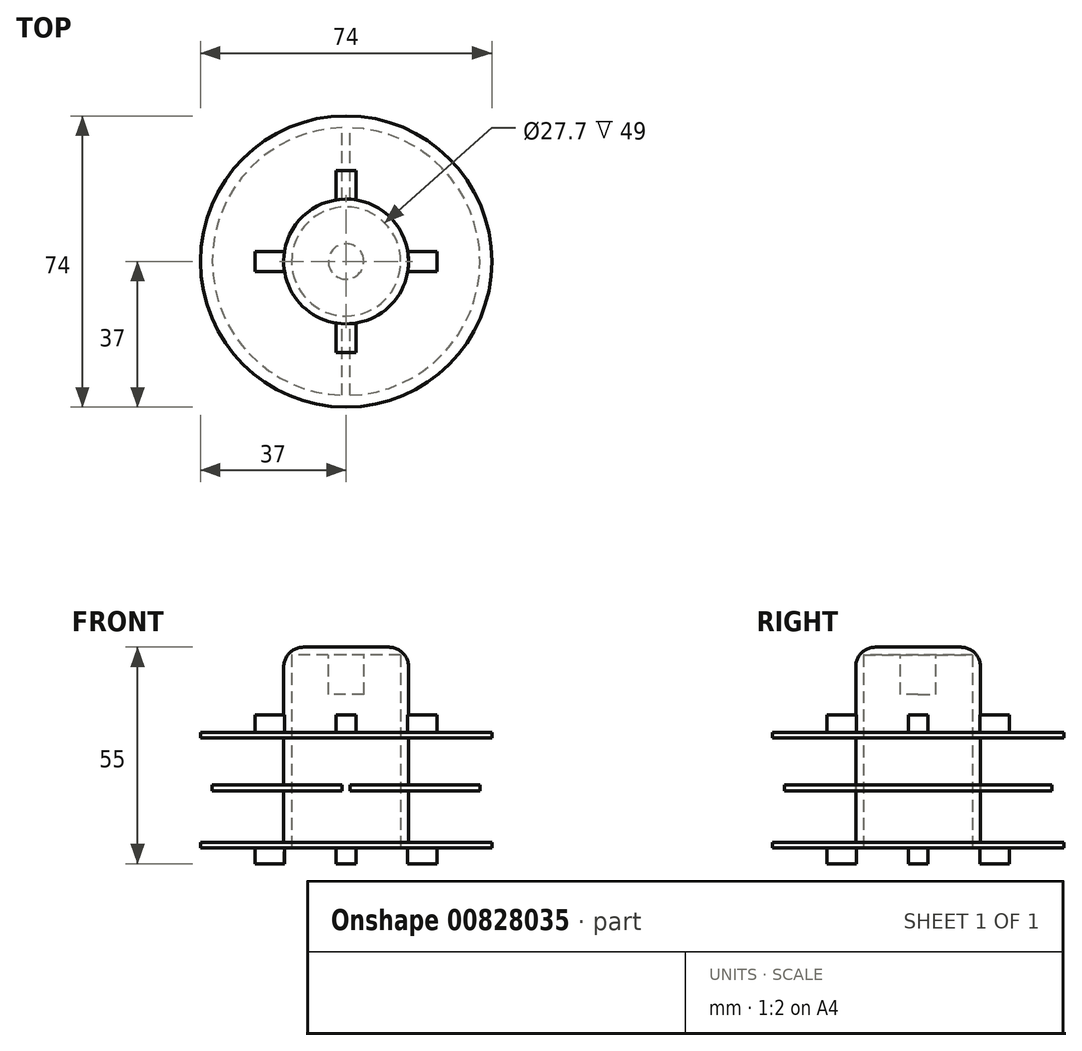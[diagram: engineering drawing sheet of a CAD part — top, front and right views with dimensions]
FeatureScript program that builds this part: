
annotation { "Feature Type Name" : "Feature", "Feature Type Description" : "" }
export const myFeature = defineFeature(function(context is Context, id is Id, definition is map)
    precondition{}
    {
        {
            var Q0;
            Q0=qCreatedBy(makeId("Top.planeOp"),FACE);
            var sketch = newSketch(context, id + "F0", { "sketchPlane" : qUnion([Q0])});
            skCircle(sketch, "E0", {"center": v(0, 0) * mm, "radius": 37 * mm});
            skCircle(sketch, "E1.0", {"center": v(0, 0) * mm, "radius": 34 * mm});
            skCircle(sketch, "E2", {"center": v(0, 0) * mm, "radius": 15.85 * mm});
            skLineSegment(sketch, "E3.top", {"start": v(0, 23.13) * mm, "end": v(-2.5, 23.13) * mm});
            skLineSegment(sketch, "E3.right", {"start": v(-2.5, 15.65) * mm, "end": v(-2.5, 23.13) * mm});
            skLineSegment(sketch, "E4.MirrorCS", {"start": v(0, 23.13) * mm, "end": v(2.5, 23.13) * mm});
            skLineSegment(sketch, "E5.MirrorCS", {"start": v(2.5, 15.65) * mm, "end": v(2.5, 23.13) * mm});
            skLineSegment(sketch, "E6.1.0", {"start": v(-15.65, -2.5) * mm, "end": v(-23.13, -2.5) * mm});
            skLineSegment(sketch, "E6.1.1", {"start": v(-23.13, 0) * mm, "end": v(-23.13, -2.5) * mm});
            skLineSegment(sketch, "E6.1.2", {"start": v(-23.13, 0) * mm, "end": v(-23.13, 2.5) * mm});
            skLineSegment(sketch, "E6.1.3", {"start": v(-15.65, 2.5) * mm, "end": v(-23.13, 2.5) * mm});
            skLineSegment(sketch, "E6.2.0", {"start": v(2.5, -15.65) * mm, "end": v(2.5, -23.13) * mm});
            skLineSegment(sketch, "E6.2.1", {"start": v(0, -23.13) * mm, "end": v(2.5, -23.13) * mm});
            skLineSegment(sketch, "E6.2.2", {"start": v(0, -23.13) * mm, "end": v(-2.5, -23.13) * mm});
            skLineSegment(sketch, "E6.2.3", {"start": v(-2.5, -15.65) * mm, "end": v(-2.5, -23.13) * mm});
            skLineSegment(sketch, "E6.3.0", {"start": v(15.65, 2.5) * mm, "end": v(23.13, 2.5) * mm});
            skLineSegment(sketch, "E6.3.1", {"start": v(23.13, 0) * mm, "end": v(23.13, 2.5) * mm});
            skLineSegment(sketch, "E6.3.2", {"start": v(23.13, 0) * mm, "end": v(23.13, -2.5) * mm});
            skLineSegment(sketch, "E6.3.3", {"start": v(15.65, -2.5) * mm, "end": v(23.13, -2.5) * mm});
            skPoint(sketch, "E7.orphan", {"position": v(-2.5, 15.85) * mm});
            skPoint(sketch, "E8.orphan", {"position": v(2.5, 15.85) * mm});
            skPoint(sketch, "E9.orphan", {"position": v(15.85, 2.5) * mm});
            skPoint(sketch, "E10.orphan", {"position": v(-15.85, 2.5) * mm});
            skPoint(sketch, "E11.orphan", {"position": v(-15.85, -2.5) * mm});
            skPoint(sketch, "E12.orphan", {"position": v(-2.5, -15.85) * mm});
            skPoint(sketch, "E13.orphan", {"position": v(2.5, -15.85) * mm});
            skPoint(sketch, "E14.orphan", {"position": v(15.85, -2.5) * mm});
            skSolve(sketch);
        }
        {
            var Q0;
            {var subQ0=sQuery(id+"F0.wireOp",EDGE,"E2");var subQ4=makeQuery(id+"F0.imprint","INTERSECT",VERTEX,{"derivedFrom":[subQ0,sQuery(id+"F0.wireOp",EDGE,"E5.MirrorCS")]});Q0=makeQuery(id+"F0.imprint","IMPRINT",FACE,{"disambiguationData":[TD([[makeQuery(id+"F0.imprint","IMPRINT",EDGE,{"disambiguationData":[TD([[subQ4,1.0]])],"derivedFrom":subQ0}),1.0]])]});}
            extrude(context, id + "F1", {"entities" : qUnion([Q0]), "depth" : 51 * mm, "offsetDistance" : 25 * mm});
        }
        {
            var Q0;
            Q0=makeQuery(id+"F0.imprint","IMPRINT",FACE,{"disambiguationData":[TD([[makeQuery(id+"F0.imprint","IMPRINT",EDGE,{"derivedFrom":sQuery(id+"F0.wireOp",EDGE,"E0")}),1.0]])]});
            var Q1;
            Q1=makeQuery(id+"F0.imprint","IMPRINT",FACE,{"disambiguationData":[TD([[makeQuery(id+"F0.imprint","IMPRINT",EDGE,{"derivedFrom":sQuery(id+"F0.wireOp",EDGE,"E1.0")}),1.0]])]});
            var Q2;
            {var subQ0=sQuery(id+"F0.wireOp",EDGE,"E6.1.0");Q2=makeQuery(id+"F0.imprint","IMPRINT",FACE,{"disambiguationData":[TD([[makeQuery(id+"F0.imprint","IMPRINT",EDGE,{"derivedFrom":subQ0}),-1.0]])]});}
            var Q3;
            Q3=makeQuery(id+"F0.imprint","IMPRINT",FACE,{"disambiguationData":[TD([[makeQuery(id+"F0.imprint","IMPRINT",EDGE,{"derivedFrom":sQuery(id+"F0.wireOp",EDGE,"E3.top")}),1.0]])]});
            var Q4;
            {var subQ0=sQuery(id+"F0.wireOp",EDGE,"E3.left");Q4=makeQuery(id+"F0.imprint","IMPRINT",FACE,{"disambiguationData":[TD([[makeQuery(id+"F0.imprint","IMPRINT",EDGE,{"derivedFrom":subQ0}),-1.0]])]});}
            var Q5;
            {var subQ0=sQuery(id+"F0.wireOp",EDGE,"E6.2.0");Q5=makeQuery(id+"F0.imprint","IMPRINT",FACE,{"disambiguationData":[TD([[makeQuery(id+"F0.imprint","IMPRINT",EDGE,{"derivedFrom":subQ0}),-1.0]])]});}
            var Q6;
            {var subQ0=sQuery(id+"F0.wireOp",EDGE,"E6.3.0");Q6=makeQuery(id+"F0.imprint","IMPRINT",FACE,{"disambiguationData":[TD([[makeQuery(id+"F0.imprint","IMPRINT",EDGE,{"derivedFrom":subQ0}),-1.0]])]});}
            extrude(context, id + "F2", {"entities" : qUnion([Q0, Q1, Q2, Q3, Q4, Q5, Q6]), "operationType" : NewBodyOperationType.ADD, "depth" : 1.4 * mm, "offsetDistance" : 25 * mm});
        }
        {
            var Q0;
            Q0=makeQuery(id+"F2.opExtrude","CAP_FACE",FACE,{"disambiguationData":[OSD([sQuery(id+"F0.wireOp",EDGE,"E0"),sQuery(id+"F0.wireOp",EDGE,"E2")])],"isStart":false});
            extrude(context, id + "F3", {"entities" : qUnion([Q0]), "operationType" : NewBodyOperationType.ADD, "depth" : 28 * mm, "offsetDistance" : 25 * mm, "hasSecondDirection" : true, "secondDirectionOppositeDirection" : false, "secondDirectionDepth" : 26.5 * mm});
        }
        {
            var Q0;
            {var subQ0=sQuery(id+"F0.wireOp",EDGE,"E6.2.0");Q0=makeQuery(id+"F0.imprint","IMPRINT",FACE,{"disambiguationData":[TD([[makeQuery(id+"F0.imprint","IMPRINT",EDGE,{"derivedFrom":subQ0}),-1.0]])]});}
            var Q1;
            {var subQ0=sQuery(id+"F0.wireOp",EDGE,"E6.3.0");Q1=makeQuery(id+"F0.imprint","IMPRINT",FACE,{"disambiguationData":[TD([[makeQuery(id+"F0.imprint","IMPRINT",EDGE,{"derivedFrom":subQ0}),-1.0]])]});}
            var Q2;
            Q2=makeQuery(id+"F0.imprint","IMPRINT",FACE,{"disambiguationData":[TD([[makeQuery(id+"F0.imprint","IMPRINT",EDGE,{"derivedFrom":sQuery(id+"F0.wireOp",EDGE,"E3.top")}),1.0]])]});
            var Q3;
            {var subQ0=sQuery(id+"F0.wireOp",EDGE,"E6.1.0");Q3=makeQuery(id+"F0.imprint","IMPRINT",FACE,{"disambiguationData":[TD([[makeQuery(id+"F0.imprint","IMPRINT",EDGE,{"derivedFrom":subQ0}),-1.0]])]});}
            extrude(context, id + "F4", {"entities" : qUnion([Q0, Q1, Q2, Q3]), "operationType" : NewBodyOperationType.ADD, "oppositeDirection" : true, "depth" : 4 * mm, "offsetDistance" : 25 * mm});
        }
        {
            var Q0;
            {var subQ0=sQuery(id+"F0.wireOp",EDGE,"E2");Q0=makeQuery(id+"F2.boolean.opBoolean","MERGE",FACE,{"derivedFrom":[makeQuery(id+"F1.opExtrude","CAP_FACE",FACE,{"disambiguationData":[OSD([subQ0])],"isStart":true}),makeQuery(id+"F2.opExtrude","CAP_FACE",FACE,{"disambiguationData":[OSD([sQuery(id+"F0.wireOp",EDGE,"E0"),subQ0])],"isStart":true})]});}
            shell(context, id + "F5", {"entities" : qUnion([Q0]), "thickness" : 2 * mm});
        }
        {
            var Q0;
            Q0=makeQuery(id+"F0.imprint","IMPRINT",FACE,{"disambiguationData":[TD([[makeQuery(id+"F0.imprint","IMPRINT",EDGE,{"derivedFrom":sQuery(id+"F0.wireOp",EDGE,"E1.0")}),1.0]])]});
            var Q1;
            {var subQ0=sQuery(id+"F0.wireOp",EDGE,"E6.3.0");Q1=makeQuery(id+"F0.imprint","IMPRINT",FACE,{"disambiguationData":[TD([[makeQuery(id+"F0.imprint","IMPRINT",EDGE,{"derivedFrom":subQ0}),-1.0]])]});}
            var Q2;
            Q2=makeQuery(id+"F0.imprint","IMPRINT",FACE,{"disambiguationData":[TD([[makeQuery(id+"F0.imprint","IMPRINT",EDGE,{"derivedFrom":sQuery(id+"F0.wireOp",EDGE,"E3.top")}),1.0]])]});
            var Q3;
            {var subQ0=sQuery(id+"F0.wireOp",EDGE,"E6.1.0");Q3=makeQuery(id+"F0.imprint","IMPRINT",FACE,{"disambiguationData":[TD([[makeQuery(id+"F0.imprint","IMPRINT",EDGE,{"derivedFrom":subQ0}),-1.0]])]});}
            var Q4;
            {var subQ0=sQuery(id+"F0.wireOp",EDGE,"E6.2.0");Q4=makeQuery(id+"F0.imprint","IMPRINT",FACE,{"disambiguationData":[TD([[makeQuery(id+"F0.imprint","IMPRINT",EDGE,{"derivedFrom":subQ0}),-1.0]])]});}
            extrude(context, id + "F6", {"entities" : qUnion([Q0, Q1, Q2, Q3, Q4]), "operationType" : NewBodyOperationType.ADD, "depth" : 16 * mm, "offsetDistance" : 25 * mm, "hasSecondDirection" : true, "secondDirectionOppositeDirection" : false, "secondDirectionDepth" : 14.5 * mm});
        }
        {
            var Q0;
            Q0=makeQuery(id+"F6.opExtrude","CAP_FACE",FACE,{"disambiguationData":[OSD([sQuery(id+"F0.wireOp",EDGE,"E1.0"),sQuery(id+"F0.wireOp",EDGE,"E2")])],"isStart":false});
            var sketch = newSketch(context, id + "F7", { "sketchPlane" : qUnion([Q0])});
            skLineSegment(sketch, "E15", {"start": v(0, 0) * mm, "end": v(0, 56.97) * mm, "construction": true});
            skLineSegment(sketch, "E16.0", {"start": v(1, -46.05) * mm, "end": v(1, 56.97) * mm});
            skLineSegment(sketch, "E17.0", {"start": v(-1, -51.76) * mm, "end": v(-1, 56.97) * mm});
            skSolve(sketch);
        }
        {
            var Q0;
            {var subQ0=sQuery(id+"F7.wireOp",EDGE,"E16.0");var subQ1=makeQuery(id+"F6.opExtrude","CAP_EDGE",EDGE,{"disambiguationData":[OSD([sQuery(id+"F0.wireOp",EDGE,"E1.0")])],"isStart":false});var subQ2=makeQuery(id+"F7.imprint","INTERSECT",VERTEX,{"disambiguationData":[OD(1.0)],"derivedFrom":[subQ1,subQ0]});Q0=makeQuery(id+"F7.imprint","IMPRINT",FACE,{"disambiguationData":[TD([[makeQuery(id+"F7.imprint","IMPRINT",EDGE,{"disambiguationData":[TD([[subQ2,1.0]])],"derivedFrom":subQ0}),1.0]])]});}
            var Q1;
            {var subQ0=sQuery(id+"F7.wireOp",EDGE,"E16.0");var subQ1=makeQuery(id+"F6.opExtrude","CAP_EDGE",EDGE,{"disambiguationData":[OSD([sQuery(id+"F0.wireOp",EDGE,"E1.0")])],"isStart":false});var subQ2=makeQuery(id+"F7.imprint","INTERSECT",VERTEX,{"disambiguationData":[OD(0.0)],"derivedFrom":[subQ1,subQ0]});Q1=makeQuery(id+"F7.imprint","IMPRINT",FACE,{"disambiguationData":[TD([[makeQuery(id+"F7.imprint","IMPRINT",EDGE,{"disambiguationData":[TD([[subQ2,-1.0]])],"derivedFrom":subQ0}),1.0]])]});}
            extrude(context, id + "F8", {"entities" : qUnion([Q0, Q1]), "operationType" : NewBodyOperationType.REMOVE, "oppositeDirection" : true, "depth" : 2 * mm, "offsetDistance" : 25 * mm});
        }
        {
            var Q0;
            {var subQ0=sQuery(id+"F0.wireOp",EDGE,"E6.2.0");Q0=makeQuery(id+"F0.imprint","IMPRINT",FACE,{"disambiguationData":[TD([[makeQuery(id+"F0.imprint","IMPRINT",EDGE,{"derivedFrom":subQ0}),-1.0]])]});}
            var Q1;
            {var subQ0=sQuery(id+"F0.wireOp",EDGE,"E6.3.0");Q1=makeQuery(id+"F0.imprint","IMPRINT",FACE,{"disambiguationData":[TD([[makeQuery(id+"F0.imprint","IMPRINT",EDGE,{"derivedFrom":subQ0}),-1.0]])]});}
            var Q2;
            Q2=makeQuery(id+"F0.imprint","IMPRINT",FACE,{"disambiguationData":[TD([[makeQuery(id+"F0.imprint","IMPRINT",EDGE,{"derivedFrom":sQuery(id+"F0.wireOp",EDGE,"E3.top")}),1.0]])]});
            var Q3;
            {var subQ0=sQuery(id+"F0.wireOp",EDGE,"E6.1.0");Q3=makeQuery(id+"F0.imprint","IMPRINT",FACE,{"disambiguationData":[TD([[makeQuery(id+"F0.imprint","IMPRINT",EDGE,{"derivedFrom":subQ0}),-1.0]])]});}
            extrude(context, id + "F9", {"entities" : qUnion([Q0, Q1, Q2, Q3]), "operationType" : NewBodyOperationType.ADD, "depth" : 33.8 * mm, "offsetDistance" : 25 * mm, "hasSecondDirection" : true, "secondDirectionOppositeDirection" : false, "secondDirectionDepth" : 28.5 * mm});
        }
        {
            var Q0;
            Q0=makeQuery(id+"F1.opExtrude","CAP_EDGE",EDGE,{"disambiguationData":[OSD([sQuery(id+"F0.wireOp",EDGE,"E2")])],"isStart":false});
            fillet(context, id + "F10", {"entities" : qUnion([Q0]), "radius" : 5 * mm, "tangentPropagation" : true, "allowEdgeOverflow" : false});
        }
        {
            var Q0;
            {var subQ0=sQuery(id+"F0.wireOp",EDGE,"E2");Q0=makeQuery(id+"F5.opShell","OFFSET_FACE",FACE,{"disambiguationData":[OSD([subQ0]),TDD([makeQuery(id+"F1.opExtrude","CAP_FACE",FACE,{"disambiguationData":[OSD([subQ0])],"isStart":false})])]});}
            var sketch = newSketch(context, id + "F11", { "sketchPlane" : qUnion([Q0])});
            skCircle(sketch, "E18", {"center": v(0, 0) * mm, "radius": 4.5 * mm});
            skSolve(sketch);
        }
        {
            var Q0;
            Q0=makeQuery(id+"F11.imprint","IMPRINT",FACE,{"disambiguationData":[TD([[makeQuery(id+"F11.imprint","IMPRINT",EDGE,{"derivedFrom":sQuery(id+"F11.wireOp",EDGE,"E18")}),1.0]])]});
            extrude(context, id + "F12", {"entities" : qUnion([Q0]), "operationType" : NewBodyOperationType.ADD, "depth" : 10 * mm, "offsetDistance" : 25 * mm});
        }
    });
